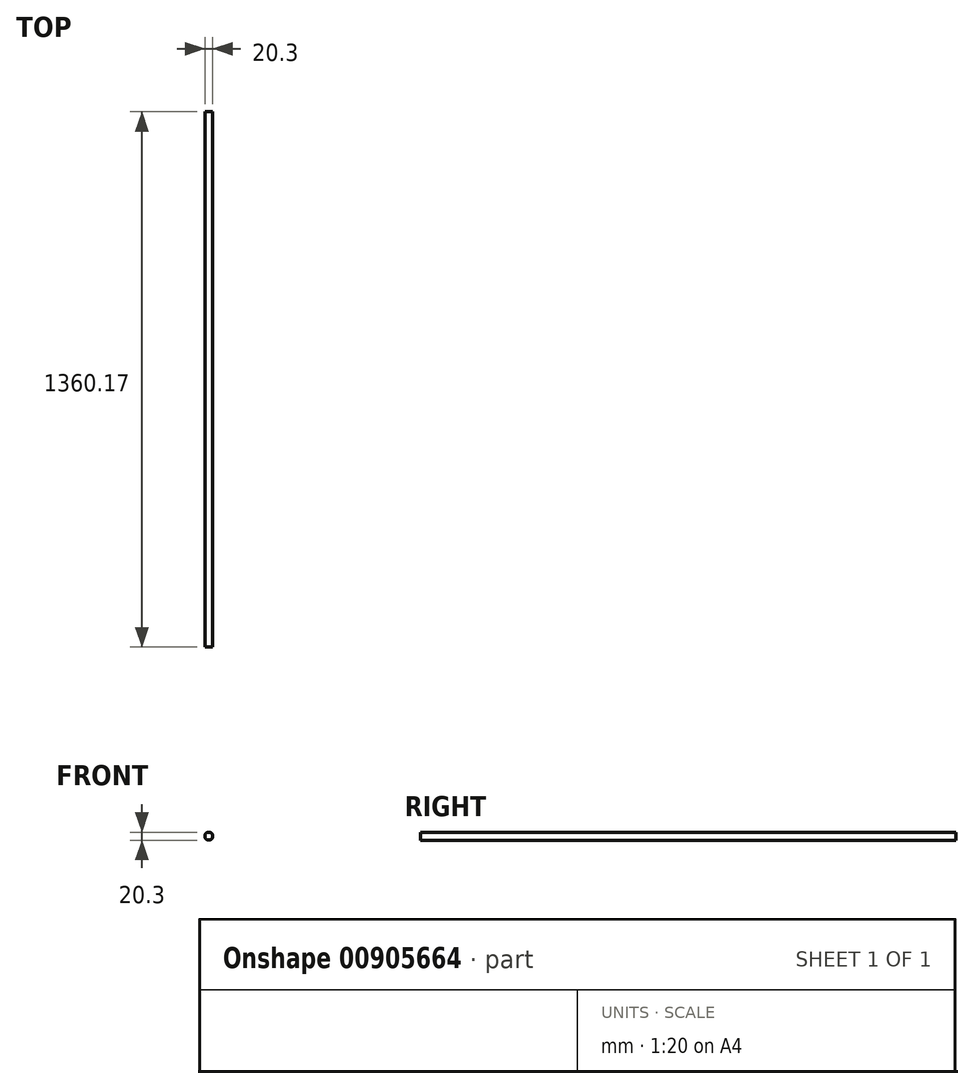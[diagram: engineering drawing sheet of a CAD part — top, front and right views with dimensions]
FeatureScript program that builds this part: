
annotation { "Feature Type Name" : "Feature", "Feature Type Description" : "" }
export const myFeature = defineFeature(function(context is Context, id is Id, definition is map)
    precondition{}
    {
        {
            var Q0;
            Q0=qCreatedBy(makeId("Front.planeOp"),FACE);
            var sketch = newSketch(context, id + "F0", { "sketchPlane" : qUnion([Q0])});
            skCircle(sketch, "E0", {"center": v(0, 0) * mm, "radius": 10.15 * mm});
            skSolve(sketch);
        }
        {
            var Q0;
            Q0 = qSketchRegion(id + "F0", true);
            extrude(context, id + "F1", {"entities" : qUnion([Q0]), "depth" : 666.75 * mm, "offsetDistance" : 25.4 * mm, "hasSecondDirection" : true, "secondDirectionOppositeDirection" : true, "secondDirectionDepth" : 693.42 * mm});
        }
    });
